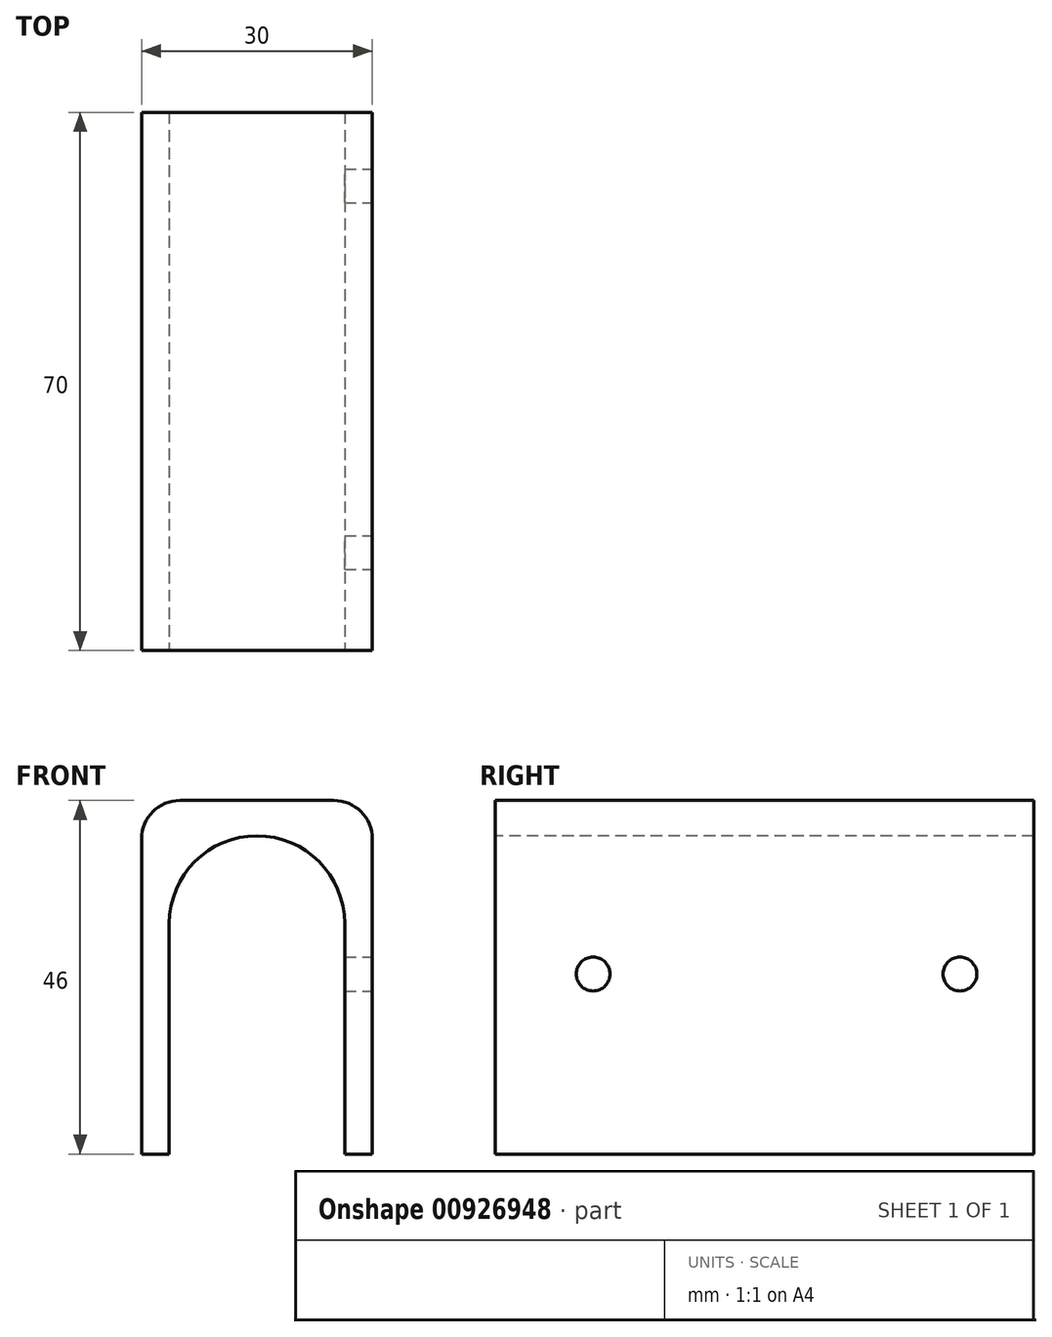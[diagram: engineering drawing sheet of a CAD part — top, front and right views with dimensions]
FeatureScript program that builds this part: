
annotation { "Feature Type Name" : "Feature", "Feature Type Description" : "" }
export const myFeature = defineFeature(function(context is Context, id is Id, definition is map)
    precondition{}
    {
        {
            var Q0;
            Q0=qCreatedBy(makeId("Front.planeOp"),FACE);
            var sketch = newSketch(context, id + "F0", { "sketchPlane" : qUnion([Q0])});
            skLineSegment(sketch, "E0.bottom", {"start": v(-50.33, 22.59) * mm, "end": v(-20.33, 22.59) * mm});
            skLineSegment(sketch, "E0.top", {"start": v(-50.33, -23.41) * mm, "end": v(-20.33, -23.41) * mm});
            skLineSegment(sketch, "E0.left", {"start": v(-50.33, 22.59) * mm, "end": v(-50.33, -23.41) * mm});
            skLineSegment(sketch, "E0.right", {"start": v(-20.33, 22.59) * mm, "end": v(-20.33, -23.41) * mm});
            skSolve(sketch);
        }
        {
            var Q0;
            Q0 = qSketchRegion(id + "F0", true);
            extrude(context, id + "F1", {"entities" : qUnion([Q0]), "depth" : 70 * mm, "offsetDistance" : 25 * mm});
        }
        {
            var Q0;
            Q0=makeQuery(id+"F1.opExtrude","CAP_FACE",FACE,{"disambiguationData":[OSD([sQuery(id+"F0.wireOp",EDGE,"E0.bottom"),sQuery(id+"F0.wireOp",EDGE,"E0.top"),sQuery(id+"F0.wireOp",EDGE,"E0.left"),sQuery(id+"F0.wireOp",EDGE,"E0.right")])],"isStart":false});
            var sketch = newSketch(context, id + "F2", { "sketchPlane" : qUnion([Q0])});
            skLineSegment(sketch, "E1.bottom", {"start": v(-46.73, -23.41) * mm, "end": v(-23.93, -23.41) * mm});
            skLineSegment(sketch, "E1.top", {"start": v(-46.73, 6.59) * mm, "end": v(-23.93, 6.59) * mm});
            skLineSegment(sketch, "E1.left", {"start": v(-46.73, -23.41) * mm, "end": v(-46.73, 6.59) * mm});
            skLineSegment(sketch, "E1.right", {"start": v(-23.93, -23.41) * mm, "end": v(-23.93, 6.59) * mm});
            skLineSegment(sketch, "E2", {"start": v(-54.42, 0) * mm, "end": v(-18.73, 0) * mm, "construction": true});
            skArc(sketch, "E3", {"start": v(-23.93, 6.59) * mm, "mid": v(-35.33, 17.99) * mm, "end": v(-46.73, 6.59) * mm});
            skSolve(sketch);
        }
        {
            var Q0;
            Q0 = qSketchRegion(id + "F2", true);
            var Q1;
            Q1 = qSketchRegion(id + "F4", true);
            extrude(context, id + "F3", {"entities" : qUnion([Q0, Q1]), "operationType" : NewBodyOperationType.REMOVE, "endBound" : BoundingType.UP_TO_NEXT, "oppositeDirection" : true, "depth" : 25 * mm, "offsetDistance" : 25 * mm});
        }
        {
            var Q0;
            Q0=makeQuery(id+"F1.opExtrude","SWEPT_FACE",FACE,{"disambiguationData":[OSD([sQuery(id+"F0.wireOp",EDGE,"E0.right")])]});
            var sketch = newSketch(context, id + "F4", { "sketchPlane" : qUnion([Q0])});
            skCircle(sketch, "E4", {"center": v(-9.58, 0) * mm, "radius": 2.2 * mm});
            skCircle(sketch, "E5", {"center": v(-57.28, 0) * mm, "radius": 2.2 * mm});
            skSolve(sketch);
        }
        {
            var Q0;
            Q0 = qSketchRegion(id + "F4", true);
            extrude(context, id + "F5", {"entities" : qUnion([Q0]), "operationType" : NewBodyOperationType.REMOVE, "endBound" : BoundingType.UP_TO_NEXT, "oppositeDirection" : true, "depth" : 25 * mm, "offsetDistance" : 25 * mm});
        }
        {
            var Q0;
            Q0=makeQuery(id+"F1.opExtrude","SWEPT_EDGE",EDGE,{"disambiguationData":[OSD([sQuery(id+"F0.wireOp",EDGE,"E0.bottom"),sQuery(id+"F0.wireOp",EDGE,"E0.right")])]});
            var Q1;
            Q1=makeQuery(id+"F1.opExtrude","SWEPT_EDGE",EDGE,{"disambiguationData":[OSD([sQuery(id+"F0.wireOp",EDGE,"E0.bottom"),sQuery(id+"F0.wireOp",EDGE,"E0.left")])]});
            fillet(context, id + "F6", {"entities" : qUnion([Q0, Q1]), "radius" : 5 * mm, "tangentPropagation" : true, "allowEdgeOverflow" : false});
        }
    });
